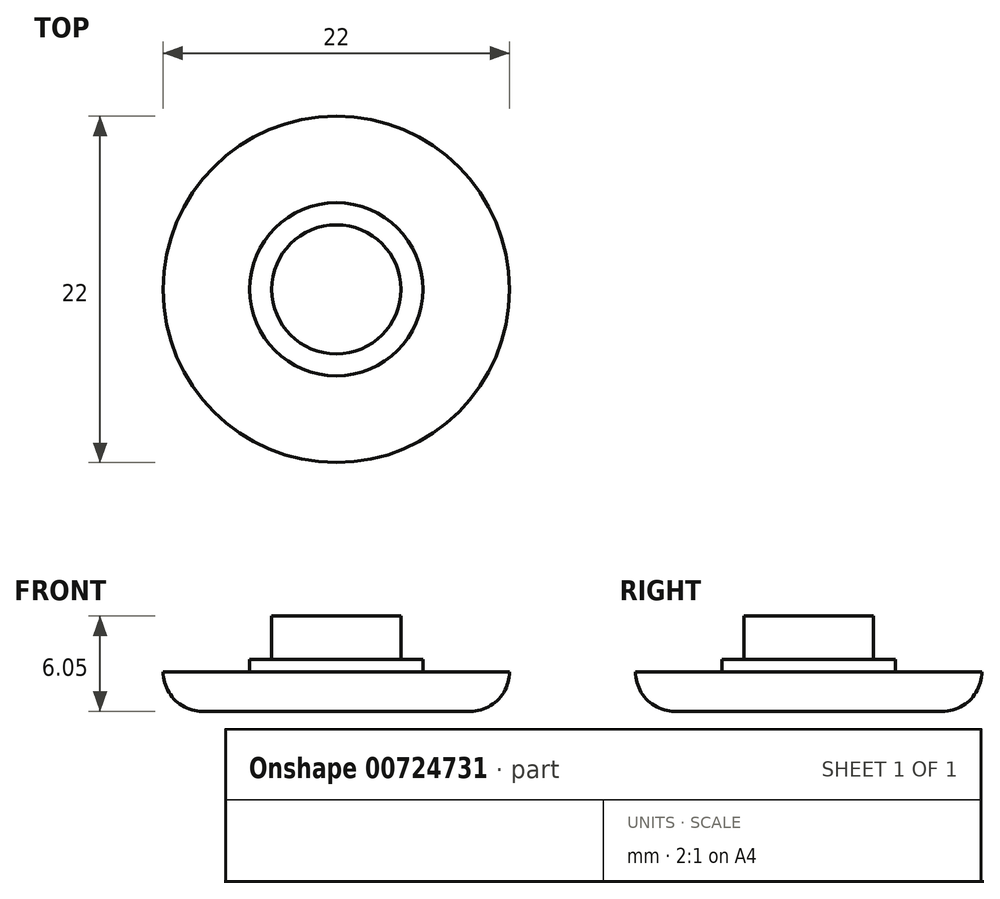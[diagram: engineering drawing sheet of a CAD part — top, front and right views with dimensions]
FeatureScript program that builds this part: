
annotation { "Feature Type Name" : "Feature", "Feature Type Description" : "" }
export const myFeature = defineFeature(function(context is Context, id is Id, definition is map)
    precondition{}
    {
        {
            var Q0;
            Q0=qCreatedBy(makeId("Top.planeOp"),FACE);
            var sketch = newSketch(context, id + "F0", { "sketchPlane" : qUnion([Q0])});
            skCircle(sketch, "E0", {"center": v(0, 0) * mm, "radius": 11 * mm});
            skCircle(sketch, "E1", {"center": v(0, 0) * mm, "radius": 4.1 * mm});
            skCircle(sketch, "E2", {"center": v(0, 0) * mm, "radius": 5.5 * mm});
            skSolve(sketch);
        }
        {
            var Q0;
            Q0=makeQuery(id+"F0.imprint","IMPRINT",FACE,{"disambiguationData":[TD([[makeQuery(id+"F0.imprint","IMPRINT",EDGE,{"derivedFrom":sQuery(id+"F0.wireOp",EDGE,"E0")}),1.0]])]});
            extrude(context, id + "F1", {"entities" : qUnion([Q0]), "depth" : 2.5 * mm, "offsetDistance" : 25 * mm});
        }
        {
            var Q0;
            Q0=makeQuery(id+"F0.imprint","IMPRINT",FACE,{"disambiguationData":[TD([[makeQuery(id+"F0.imprint","IMPRINT",EDGE,{"derivedFrom":sQuery(id+"F0.wireOp",EDGE,"E1")}),-1.0]])]});
            var Q1;
            Q1=makeQuery(id+"F1.opExtrude","CAP_FACE",FACE,{"disambiguationData":[OSD([sQuery(id+"F0.wireOp",EDGE,"E0"),sQuery(id+"F0.wireOp",EDGE,"E2")])],"isStart":false});
            extrude(context, id + "F2", {"entities" : qUnion([Q0]), "operationType" : NewBodyOperationType.ADD, "endBound" : BoundingType.UP_TO_SURFACE, "depth" : 25 * mm, "endBoundEntityFace" : qUnion([Q1]), "hasOffset" : true, "offsetDistance" : .8 * mm, "offsetOppositeDirection" : true});
        }
        {
            var Q0;
            Q0=makeQuery(id+"F0.imprint","IMPRINT",FACE,{"disambiguationData":[TD([[makeQuery(id+"F0.imprint","IMPRINT",EDGE,{"derivedFrom":sQuery(id+"F0.wireOp",EDGE,"E1")}),1.0]])]});
            var Q1;
            Q1=makeQuery(id+"F2.opExtrude","CAP_FACE",FACE,{"disambiguationData":[OSD([sQuery(id+"F0.wireOp",EDGE,"E0"),sQuery(id+"F0.wireOp",EDGE,"E2")])],"isStart":false});
            extrude(context, id + "F3", {"entities" : qUnion([Q0]), "operationType" : NewBodyOperationType.ADD, "endBound" : BoundingType.UP_TO_SURFACE, "depth" : 3 * mm, "endBoundEntityFace" : qUnion([Q1]), "hasOffset" : true, "offsetDistance" : 2.75 * mm, "offsetOppositeDirection" : true});
        }
        {
            var Q0;
            {var subQ0=sQuery(id+"F0.wireOp",EDGE,"E1");var subQ1=sQuery(id+"F0.wireOp",EDGE,"E2");Q0=makeQuery(id+"F3.boolean.opBoolean","MERGE",FACE,{"derivedFrom":[makeQuery(id+"F2.boolean.opBoolean","MERGE",FACE,{"derivedFrom":[makeQuery(id+"F1.opExtrude","CAP_FACE",FACE,{"disambiguationData":[OSD([sQuery(id+"F0.wireOp",EDGE,"E0"),subQ1])],"isStart":true}),makeQuery(id+"F2.opExtrude","CAP_FACE",FACE,{"disambiguationData":[OSD([subQ0,subQ1])],"isStart":true})]}),makeQuery(id+"F3.opExtrude","CAP_FACE",FACE,{"disambiguationData":[OSD([subQ0])],"isStart":true})]});}
            fillet(context, id + "F4", {"entities" : qUnion([Q0]), "radius" : 2.5 * mm, "tangentPropagation" : true, "allowEdgeOverflow" : false});
        }
    });
